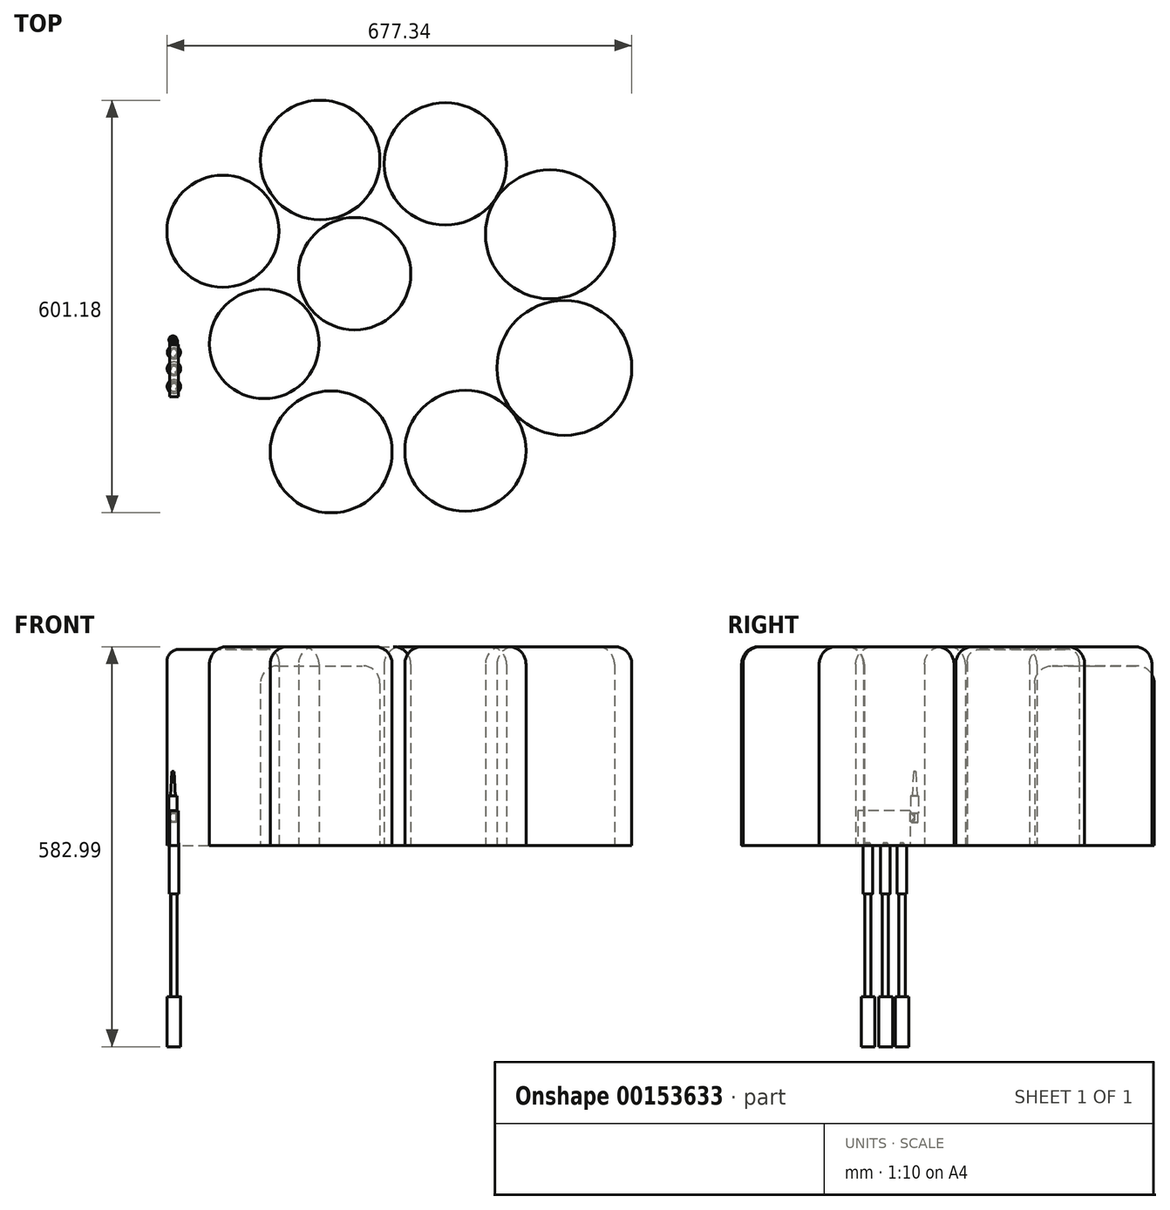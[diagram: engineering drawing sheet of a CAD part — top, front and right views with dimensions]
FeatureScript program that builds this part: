
annotation { "Feature Type Name" : "Feature", "Feature Type Description" : "" }
export const myFeature = defineFeature(function(context is Context, id is Id, definition is map)
    precondition{}
    {
        {
            var Q0;
            Q0=qCreatedBy(makeId("Front.planeOp"),FACE);
            var sketch = newSketch(context, id + "F0", { "sketchPlane" : qUnion([Q0])});
            skLineSegment(sketch, "E0.bottom", {"start": v(0, 0) * mm, "end": v(359.7, 0) * mm});
            skLineSegment(sketch, "E0.top", {"start": v(0, 54.03) * mm, "end": v(359.7, 54.03) * mm});
            skLineSegment(sketch, "E0.left", {"start": v(0, 0) * mm, "end": v(0, 54.03) * mm});
            skArc(sketch, "E1", {"start": v(359.7, 0) * mm, "mid": v(558.37, 27.02) * mm, "end": v(359.7, 54.03) * mm});
            skSolve(sketch);
        }
        {
            var Q0;
            Q0=sQuery(id+"F0.wireOp",EDGE,"E1");
            var Q1;
            Q1=sQuery(id+"F0.wireOp",EDGE,"E0.top");
            var Q2;
            Q2=sQuery(id+"F0.wireOp",EDGE,"E0.bottom");
            var Q3;
            Q3=sQuery(id+"F0.wireOp",EDGE,"E0.left");
            revolve(context, id + "F1", {"bodyType" : ToolBodyType.SURFACE, "surfaceEntities" : qUnion([Q0, Q1, Q2]), "axis" : qUnion([Q3]), "revolveType" : RevolveType.FULL});
        }
        {
            var Q0;
            Q0=makeQuery(id+"F1.opRevolve","SWEPT_FACE",FACE,{"disambiguationData":[OSD([sQuery(id+"F0.wireOp",EDGE,"E0.top")])]});
            var sketch = newSketch(context, id + "F2", { "sketchPlane" : qUnion([Q0])});
            skLineSegment(sketch, "E2.bottom", {"start": v(-334.16, 133.13) * mm, "end": v(-321.46, 133.13) * mm});
            skLineSegment(sketch, "E2.top", {"start": v(-334.16, 56.93) * mm, "end": v(-321.46, 56.93) * mm});
            skLineSegment(sketch, "E2.left", {"start": v(-334.16, 56.93) * mm, "end": v(-334.16, 133.13) * mm});
            skLineSegment(sketch, "E2.right", {"start": v(-321.46, 56.93) * mm, "end": v(-321.46, 133.13) * mm});
            skSolve(sketch);
        }
        {
            var Q0;
            Q0 = qSketchRegion(id + "F2", true);
            extrude(context, id + "F3", {"entities" : qUnion([Q0]), "oppositeDirection" : true, "depth" : 50.8 * mm});
        }
        {
            var Q0;
            Q0=makeQuery(id+"F3.opExtrude","SWEPT_FACE",FACE,{"disambiguationData":[OSD([sQuery(id+"F2.wireOp",EDGE,"E2.top")])]});
            var sketch = newSketch(context, id + "F4", { "sketchPlane" : qUnion([Q0])});
            skCircle(sketch, "E3", {"center": v(328.27, 94.76) * mm, "radius": 5.86 * mm});
            skSolve(sketch);
        }
        {
            var Q0;
            Q0 = qSketchRegion(id + "F4", true);
            extrude(context, id + "F5", {"entities" : qUnion([Q0]), "operationType" : NewBodyOperationType.ADD, "depth" : 6.35 * mm});
        }
        {
            var Q0;
            Q0=makeQuery(id+"F5.opExtrude","CAP_FACE",FACE,{"disambiguationData":[OSD([sQuery(id+"F4.wireOp",EDGE,"E3")])],"isStart":false});
            var sketch = newSketch(context, id + "F6", { "sketchPlane" : qUnion([Q0])});
            skLineSegment(sketch, "E4.bottom", {"start": v(329.22, 100.54) * mm, "end": v(333.95, 100.54) * mm});
            skLineSegment(sketch, "E4.top", {"start": v(329.22, 87.7) * mm, "end": v(333.95, 87.7) * mm});
            skLineSegment(sketch, "E4.left", {"start": v(329.22, 100.54) * mm, "end": v(329.22, 87.7) * mm});
            skLineSegment(sketch, "E4.right", {"start": v(333.95, 100.54) * mm, "end": v(333.95, 87.7) * mm});
            skSolve(sketch);
        }
        {
            var Q0;
            {var subQ0=sQuery(id+"F6.wireOp",EDGE,"E4.bottom");Q0=makeQuery(id+"F6.imprint","IMPRINT",FACE,{"disambiguationData":[TD([[makeQuery(id+"F6.imprint","IMPRINT",EDGE,{"derivedFrom":subQ0}),-1.0]])]});}
            var Q1;
            {var subQ0=sQuery(id+"F6.wireOp",EDGE,"E4.top");Q1=makeQuery(id+"F6.imprint","IMPRINT",FACE,{"disambiguationData":[TD([[makeQuery(id+"F6.imprint","IMPRINT",EDGE,{"derivedFrom":subQ0}),1.0]])]});}
            var Q2;
            {var subQ1=makeQuery(id+"F5.opExtrude","CAP_EDGE",EDGE,{"disambiguationData":[OSD([sQuery(id+"F4.wireOp",EDGE,"E3")])],"isStart":false});var subQ4=sQuery(id+"F6.wireOp",EDGE,"E4.right");var subQ6=makeQuery(id+"F6.imprint","INTERSECT",VERTEX,{"disambiguationData":[OD(0.0)],"derivedFrom":[subQ1,subQ4]});Q2=makeQuery(id+"F6.imprint","IMPRINT",FACE,{"disambiguationData":[TD([[makeQuery(id+"F6.imprint","IMPRINT",EDGE,{"disambiguationData":[TD([[subQ6,-1.0]])],"derivedFrom":subQ4}),-1.0]])]});}
            var Q3;
            Q3=sQuery(id+"F6.wireOp",EDGE,"E4.left");
            revolve(context, id + "F7", {"operationType" : NewBodyOperationType.ADD, "entities" : qUnion([Q0, Q1, Q2]), "axis" : qUnion([Q3]), "revolveType" : RevolveType.FULL});
        }
        {
            var Q0;
            Q0=makeQuery(id+"F7.opRevolve","SWEPT_FACE",FACE,{"disambiguationData":[OSD([sQuery(id+"F6.wireOp",EDGE,"E4.bottom")])]});
            var sketch = newSketch(context, id + "F8", { "sketchPlane" : qUnion([Q0])});
            skCircle(sketch, "E5", {"center": v(-329.22, -50.58) * mm, "radius": 5.84 * mm});
            skSolve(sketch);
        }
        {
            var Q0;
            Q0 = qSketchRegion(id + "F8", true);
            extrude(context, id + "F9", {"entities" : qUnion([Q0]), "operationType" : NewBodyOperationType.ADD, "depth" : 25.4 * mm});
        }
        {
            var Q0;
            Q0=makeQuery(id+"F9.opExtrude","CAP_FACE",FACE,{"disambiguationData":[OSD([sQuery(id+"F8.wireOp",EDGE,"E5")])],"isStart":false});
            var sketch = newSketch(context, id + "F10", { "sketchPlane" : qUnion([Q0])});
            skCircle(sketch, "E6", {"center": v(-329.22, -50.58) * mm, "radius": 3.46 * mm});
            skSolve(sketch);
        }
        {
            var Q0;
            Q0 = qSketchRegion(id + "F10", true);
            extrude(context, id + "F11", {"entities" : qUnion([Q0]), "operationType" : NewBodyOperationType.ADD, "depth" : 35.56 * mm, "hasDraft" : true, "draftAngle" : 3 * degree, "draftPullDirection" : true});
        }
        {
            var Q0;
            Q0=makeQuery(id+"F1.opRevolve","SWEPT_FACE",FACE,{"disambiguationData":[OSD([sQuery(id+"F0.wireOp",EDGE,"E0.bottom")])]});
            var sketch = newSketch(context, id + "F12", { "sketchPlane" : qUnion([Q0])});
            skCircle(sketch, "E7", {"center": v(-327.78, -118.48) * mm, "radius": 7.03 * mm});
            skCircle(sketch, "E8", {"center": v(-327.78, -93.25) * mm, "radius": 7.03 * mm});
            skCircle(sketch, "E9", {"center": v(-327.78, -69.13) * mm, "radius": 6.72 * mm});
            skSolve(sketch);
        }
        {
            var Q0;
            Q0 = qSketchRegion(id + "F12", true);
            extrude(context, id + "F13", {"entities" : qUnion([Q0]), "operationType" : NewBodyOperationType.ADD, "depth" : 57.78 * mm, "hasSecondDirection" : true, "secondDirectionOppositeDirection" : true, "secondDirectionDepth" : 16.5 * mm});
        }
        {
            var Q0;
            Q0=makeQuery(id+"F13.opExtrude","CAP_FACE",FACE,{"disambiguationData":[OSD([sQuery(id+"F12.wireOp",EDGE,"E7")])],"isStart":true});
            var sketch = newSketch(context, id + "F14", { "sketchPlane" : qUnion([Q0])});
            skCircle(sketch, "E10", {"center": v(-327.78, 118.48) * mm, "radius": 4.46 * mm});
            skCircle(sketch, "E11", {"center": v(-327.78, 93.38) * mm, "radius": 4.52 * mm});
            skCircle(sketch, "E12", {"center": v(-327.95, 68.93) * mm, "radius": 4.64 * mm});
            skSolve(sketch);
        }
        {
            var Q0;
            Q0=makeQuery(id+"F14.imprint","IMPRINT",FACE,{"disambiguationData":[TD([[makeQuery(id+"F14.imprint","IMPRINT",EDGE,{"derivedFrom":sQuery(id+"F14.wireOp",EDGE,"E10")}),1.0]])]});
            var Q1;
            Q1=makeQuery(id+"F14.imprint","IMPRINT",FACE,{"disambiguationData":[TD([[makeQuery(id+"F14.imprint","IMPRINT",EDGE,{"derivedFrom":sQuery(id+"F14.wireOp",EDGE,"E11")}),1.0]])]});
            var Q2;
            Q2=makeQuery(id+"F14.imprint","IMPRINT",FACE,{"disambiguationData":[TD([[makeQuery(id+"F14.imprint","IMPRINT",EDGE,{"derivedFrom":sQuery(id+"F14.wireOp",EDGE,"E12")}),1.0]])]});
            extrude(context, id + "F15", {"entities" : qUnion([Q0, Q1, Q2]), "operationType" : NewBodyOperationType.ADD, "depth" : 149.86 * mm});
        }
        {
            var Q0;
            Q0=makeQuery(id+"F15.opExtrude","CAP_FACE",FACE,{"disambiguationData":[OSD([sQuery(id+"F14.wireOp",EDGE,"E10")])],"isStart":false});
            var sketch = newSketch(context, id + "F16", { "sketchPlane" : qUnion([Q0])});
            skCircle(sketch, "E13", {"center": v(-327.78, 118.48) * mm, "radius": 9.83 * mm});
            skCircle(sketch, "E14", {"center": v(-327.78, 92.57) * mm, "radius": 9.92 * mm});
            skCircle(sketch, "E15", {"center": v(-327.78, 68.67) * mm, "radius": 9.65 * mm});
            skSolve(sketch);
        }
        {
            var Q0;
            Q0 = qSketchRegion(id + "F16", true);
            extrude(context, id + "F17", {"entities" : qUnion([Q0]), "operationType" : NewBodyOperationType.ADD, "depth" : 73.02 * mm});
        }
        {
            var Q0;
            Q0=makeQuery(id+"F1.opRevolve","SWEPT_FACE",FACE,{"disambiguationData":[OSD([sQuery(id+"F0.wireOp",EDGE,"E0.top")])]});
            var sketch = newSketch(context, id + "F18", { "sketchPlane" : qUnion([Q0])});
            skCircle(sketch, "E16", {"center": v(-256.32, -107.82) * mm, "radius": 81.62 * mm});
            skSolve(sketch);
        }
        {
            var Q0;
            Q0 = qSketchRegion(id + "F18", true);
            extrude(context, id + "F19", {"entities" : qUnion([Q0]), "oppositeDirection" : true, "depth" : 285.75 * mm});
        }
        {
            var Q0;
            Q0=makeQuery(id+"F19.opExtrude","CAP_EDGE",EDGE,{"disambiguationData":[OSD([sQuery(id+"F18.wireOp",EDGE,"E16")])],"isStart":false});
            fillet(context, id + "F20", {"entities" : qUnion([Q0]), "radius" : 17.78 * mm, "tangentPropagation" : true, "allowEdgeOverflow" : false});
        }
        {
            var Q0;
            Q0=makeQuery(id+"F1.opRevolve","SWEPT_FACE",FACE,{"disambiguationData":[OSD([sQuery(id+"F0.wireOp",EDGE,"E0.top")])]});
            var sketch = newSketch(context, id + "F21", { "sketchPlane" : qUnion([Q0])});
            skCircle(sketch, "E17", {"center": v(-114.68, -211.57) * mm, "radius": 87.06 * mm});
            skSolve(sketch);
        }
        {
            var Q0;
            Q0 = qSketchRegion(id + "F21", true);
            extrude(context, id + "F22", {"entities" : qUnion([Q0]), "oppositeDirection" : true, "depth" : 261.62 * mm});
        }
        {
            var Q0;
            Q0=makeQuery(id+"F1.opRevolve","SWEPT_FACE",FACE,{"disambiguationData":[OSD([sQuery(id+"F0.wireOp",EDGE,"E0.top")])]});
            var sketch = newSketch(context, id + "F23", { "sketchPlane" : qUnion([Q0])});
            skCircle(sketch, "E18", {"center": v(67.67, -206) * mm, "radius": 89.11 * mm});
            skCircle(sketch, "E19", {"center": v(220.11, -103.28) * mm, "radius": 93.97 * mm});
            skCircle(sketch, "E20", {"center": v(241.14, 91.38) * mm, "radius": 98.25 * mm});
            skCircle(sketch, "E21", {"center": v(96.87, 212.2) * mm, "radius": 88.26 * mm});
            skCircle(sketch, "E22", {"center": v(-98.65, 213.76) * mm, "radius": 88.8 * mm});
            skCircle(sketch, "E23", {"center": v(-196.2, 56.4) * mm, "radius": 79.81 * mm});
            skCircle(sketch, "E24", {"center": v(-64.55, -45.9) * mm, "radius": 81.81 * mm});
            skSolve(sketch);
        }
        {
            var Q0;
            Q0=makeQuery(id+"F23.imprint","IMPRINT",FACE,{"disambiguationData":[TD([[makeQuery(id+"F23.imprint","IMPRINT",EDGE,{"derivedFrom":sQuery(id+"F23.wireOp",EDGE,"E18")}),1.0]])]});
            var Q1;
            Q1=makeQuery(id+"F23.imprint","IMPRINT",FACE,{"disambiguationData":[TD([[makeQuery(id+"F23.imprint","IMPRINT",EDGE,{"derivedFrom":sQuery(id+"F23.wireOp",EDGE,"E19")}),1.0]])]});
            var Q2;
            Q2=makeQuery(id+"F23.imprint","IMPRINT",FACE,{"disambiguationData":[TD([[makeQuery(id+"F23.imprint","IMPRINT",EDGE,{"derivedFrom":sQuery(id+"F23.wireOp",EDGE,"E20")}),1.0]])]});
            var Q3;
            Q3=makeQuery(id+"F23.imprint","IMPRINT",FACE,{"disambiguationData":[TD([[makeQuery(id+"F23.imprint","IMPRINT",EDGE,{"derivedFrom":sQuery(id+"F23.wireOp",EDGE,"E21")}),1.0]])]});
            var Q4;
            Q4=makeQuery(id+"F23.imprint","IMPRINT",FACE,{"disambiguationData":[TD([[makeQuery(id+"F23.imprint","IMPRINT",EDGE,{"derivedFrom":sQuery(id+"F23.wireOp",EDGE,"E22")}),1.0]])]});
            var Q5;
            Q5=makeQuery(id+"F23.imprint","IMPRINT",FACE,{"disambiguationData":[TD([[makeQuery(id+"F23.imprint","IMPRINT",EDGE,{"derivedFrom":sQuery(id+"F23.wireOp",EDGE,"E24")}),1.0]])]});
            var Q6;
            Q6=makeQuery(id+"F23.imprint","IMPRINT",FACE,{"disambiguationData":[TD([[makeQuery(id+"F23.imprint","IMPRINT",EDGE,{"derivedFrom":sQuery(id+"F23.wireOp",EDGE,"E23")}),1.0]])]});
            extrude(context, id + "F24", {"entities" : qUnion([Q0, Q1, Q2, Q3, Q4, Q5, Q6]), "oppositeDirection" : true, "depth" : 289.56 * mm});
        }
        {
            var Q0;
            Q0=makeQuery(id+"F24.opExtrude","CAP_FACE",FACE,{"disambiguationData":[OSD([sQuery(id+"F23.wireOp",EDGE,"E22")])],"isStart":false});
            var Q1;
            Q1=makeQuery(id+"F24.opExtrude","CAP_FACE",FACE,{"disambiguationData":[OSD([sQuery(id+"F23.wireOp",EDGE,"E23")])],"isStart":false});
            var Q2;
            Q2=makeQuery(id+"F24.opExtrude","CAP_FACE",FACE,{"disambiguationData":[OSD([sQuery(id+"F23.wireOp",EDGE,"E24")])],"isStart":false});
            var Q3;
            Q3=makeQuery(id+"F22.opExtrude","CAP_FACE",FACE,{"disambiguationData":[OSD([sQuery(id+"F21.wireOp",EDGE,"E17")])],"isStart":false});
            var Q4;
            Q4=makeQuery(id+"F24.opExtrude","CAP_FACE",FACE,{"disambiguationData":[OSD([sQuery(id+"F23.wireOp",EDGE,"E18")])],"isStart":false});
            var Q5;
            Q5=makeQuery(id+"F24.opExtrude","CAP_FACE",FACE,{"disambiguationData":[OSD([sQuery(id+"F23.wireOp",EDGE,"E19")])],"isStart":false});
            var Q6;
            Q6=makeQuery(id+"F24.opExtrude","CAP_FACE",FACE,{"disambiguationData":[OSD([sQuery(id+"F23.wireOp",EDGE,"E20")])],"isStart":false});
            var Q7;
            Q7=makeQuery(id+"F24.opExtrude","CAP_FACE",FACE,{"disambiguationData":[OSD([sQuery(id+"F23.wireOp",EDGE,"E21")])],"isStart":false});
            fillet(context, id + "F25", {"entities" : qUnion([Q0, Q1, Q2, Q3, Q4, Q5, Q6, Q7]), "radius" : 25.4 * mm, "tangentPropagation" : true, "allowEdgeOverflow" : false});
        }
    });
